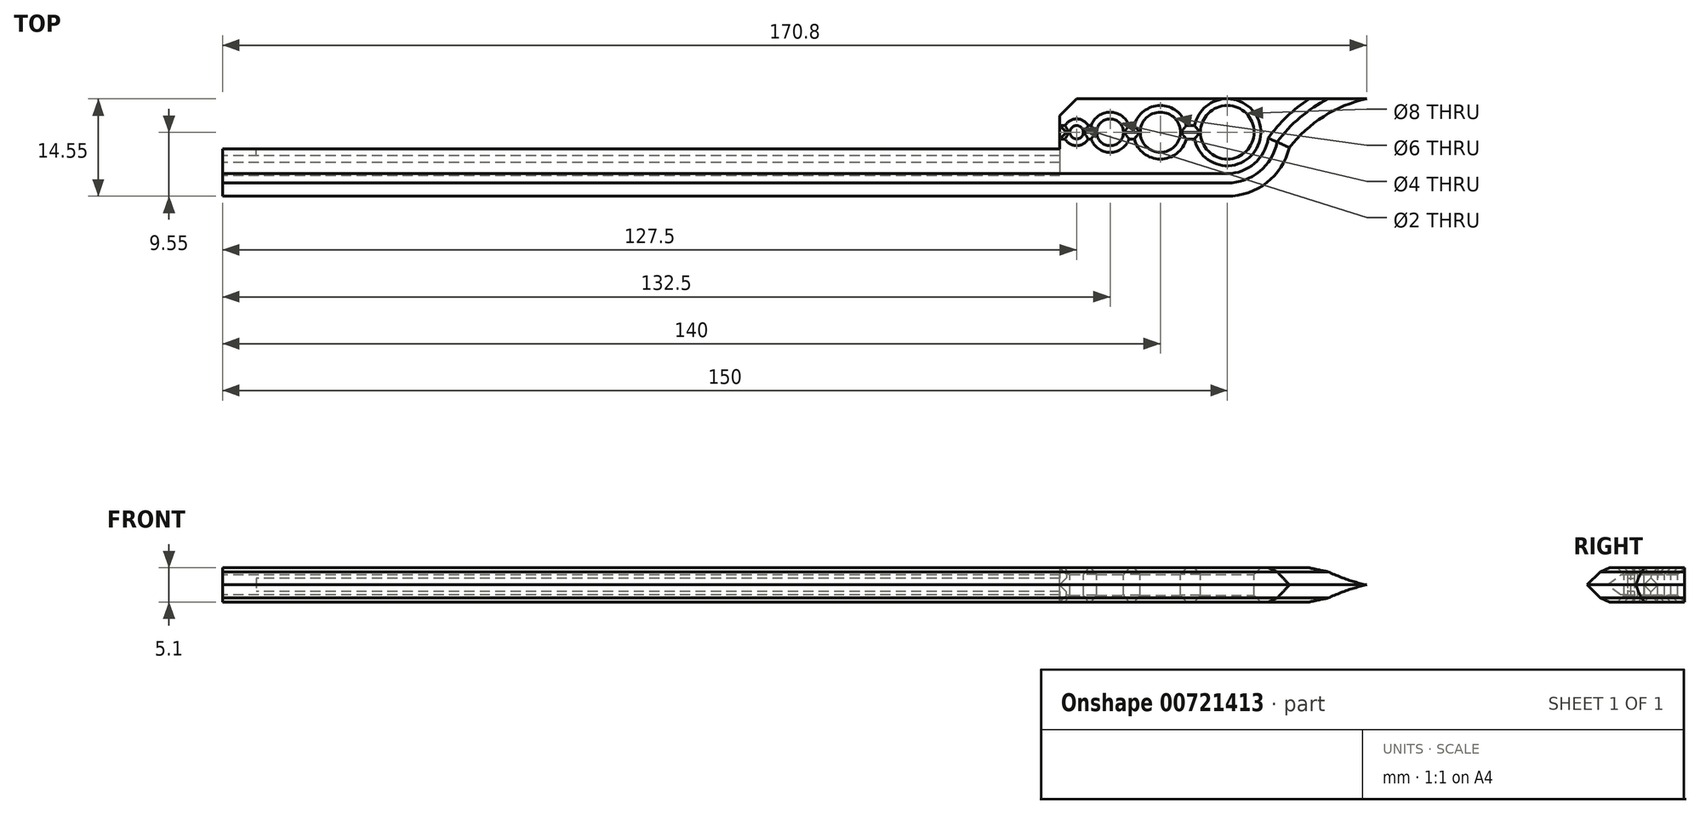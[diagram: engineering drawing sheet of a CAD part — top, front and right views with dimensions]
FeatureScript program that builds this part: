
annotation { "Feature Type Name" : "Feature", "Feature Type Description" : "" }
export const myFeature = defineFeature(function(context is Context, id is Id, definition is map)
    precondition{}
    {
        {
            var Q0;
            Q0=qCreatedBy(makeId("Top.planeOp"),FACE);
            var sketch = newSketch(context, id + "F0", { "sketchPlane" : qUnion([Q0])});
            skLineSegment(sketch, "E0.bottom", {"start": v(125, 0) * mm, "end": v(175, 0) * mm});
            skLineSegment(sketch, "E0.top", {"start": v(0, -15) * mm, "end": v(150, -15) * mm});
            skLineSegment(sketch, "E0.left", {"start": v(0, -7.5) * mm, "end": v(0, -15) * mm});
            skArc(sketch, "E1", {"start": v(150, -15) * mm, "mid": v(156.12, -12.9) * mm, "end": v(159.68, -7.5) * mm});
            skArc(sketch, "E2", {"start": v(175, 0) * mm, "mid": v(166.47, -1.98) * mm, "end": v(159.68, -7.5) * mm});
            skLineSegment(sketch, "E3.top", {"start": v(0, -7.5) * mm, "end": v(125, -7.5) * mm});
            skLineSegment(sketch, "E3.right", {"start": v(125, 0) * mm, "end": v(125, -7.5) * mm});
            skPoint(sketch, "E4.orphan", {"position": v(0, 0) * mm});
            skSolve(sketch);
        }
        {
            var Q0;
            Q0 = qSketchRegion(id + "F0", true);
            extrude(context, id + "F1", {"entities" : qUnion([Q0]), "depth" : 2.55 * mm, "offsetDistance" : 25 * mm});
        }
        {
            var Q0;
            Q0=makeQuery(id+"F1.opExtrude","CAP_EDGE",EDGE,{"disambiguationData":[OSD([sQuery(id+"F0.wireOp",EDGE,"E0.top")])],"isStart":false});
            var Q1;
            Q1=makeQuery(id+"F1.opExtrude","CAP_EDGE",EDGE,{"disambiguationData":[OSD([sQuery(id+"F0.wireOp",EDGE,"E1")])],"isStart":false});
            var Q2;
            Q2=makeQuery(id+"F1.opExtrude","CAP_EDGE",EDGE,{"disambiguationData":[OSD([sQuery(id+"F0.wireOp",EDGE,"E2")])],"isStart":false});
            chamfer(context, id + "F2", {"entities" : qUnion([Q0, Q1, Q2]), "width" : 3 * mm, "tangentPropagation" : true});
        }
        {
            var Q0;
            {var subQ0=sQuery(id+"F0.wireOp",EDGE,"E0.top");Q0=makeQuery(id+"F2.opChamfer","BLEND_EDGE",EDGE,{"blendedFrom":[makeQuery(id+"F1.opExtrude","CAP_EDGE",EDGE,{"disambiguationData":[OSD([subQ0])],"isStart":false}),makeQuery(id+"F1.opExtrude","CAP_FACE",FACE,{"disambiguationData":[OSD([sQuery(id+"F0.wireOp",EDGE,"E0.bottom"),subQ0,sQuery(id+"F0.wireOp",EDGE,"E0.left"),sQuery(id+"F0.wireOp",EDGE,"E1"),sQuery(id+"F0.wireOp",EDGE,"E2"),sQuery(id+"F0.wireOp",EDGE,"E3.top"),sQuery(id+"F0.wireOp",EDGE,"E3.right")])],"isStart":false})],"blendedInto":[makeQuery(id+"F1.opExtrude","CAP_FACE",FACE,{"disambiguationData":[OSD([sQuery(id+"F0.wireOp",EDGE,"E0.bottom"),subQ0,sQuery(id+"F0.wireOp",EDGE,"E0.left"),sQuery(id+"F0.wireOp",EDGE,"E1"),sQuery(id+"F0.wireOp",EDGE,"E2"),sQuery(id+"F0.wireOp",EDGE,"E3.top"),sQuery(id+"F0.wireOp",EDGE,"E3.right")])],"isStart":false})]});}
            var Q1;
            {var subQ0=sQuery(id+"F0.wireOp",EDGE,"E1");Q1=makeQuery(id+"F2.opChamfer","BLEND_EDGE",EDGE,{"blendedFrom":[makeQuery(id+"F1.opExtrude","CAP_EDGE",EDGE,{"disambiguationData":[OSD([subQ0])],"isStart":false}),makeQuery(id+"F1.opExtrude","CAP_FACE",FACE,{"disambiguationData":[OSD([sQuery(id+"F0.wireOp",EDGE,"E0.bottom"),sQuery(id+"F0.wireOp",EDGE,"E0.top"),sQuery(id+"F0.wireOp",EDGE,"E0.left"),subQ0,sQuery(id+"F0.wireOp",EDGE,"E2"),sQuery(id+"F0.wireOp",EDGE,"E3.top"),sQuery(id+"F0.wireOp",EDGE,"E3.right")])],"isStart":false})],"blendedInto":[makeQuery(id+"F1.opExtrude","CAP_FACE",FACE,{"disambiguationData":[OSD([sQuery(id+"F0.wireOp",EDGE,"E0.bottom"),sQuery(id+"F0.wireOp",EDGE,"E0.top"),sQuery(id+"F0.wireOp",EDGE,"E0.left"),subQ0,sQuery(id+"F0.wireOp",EDGE,"E2"),sQuery(id+"F0.wireOp",EDGE,"E3.top"),sQuery(id+"F0.wireOp",EDGE,"E3.right")])],"isStart":false})]});}
            var Q2;
            {var subQ0=sQuery(id+"F0.wireOp",EDGE,"E2");Q2=makeQuery(id+"F2.opChamfer","BLEND_EDGE",EDGE,{"blendedFrom":[makeQuery(id+"F1.opExtrude","CAP_EDGE",EDGE,{"disambiguationData":[OSD([subQ0])],"isStart":false}),makeQuery(id+"F1.opExtrude","CAP_FACE",FACE,{"disambiguationData":[OSD([sQuery(id+"F0.wireOp",EDGE,"E0.bottom"),sQuery(id+"F0.wireOp",EDGE,"E0.top"),sQuery(id+"F0.wireOp",EDGE,"E0.left"),sQuery(id+"F0.wireOp",EDGE,"E1"),subQ0,sQuery(id+"F0.wireOp",EDGE,"E3.top"),sQuery(id+"F0.wireOp",EDGE,"E3.right")])],"isStart":false})],"blendedInto":[makeQuery(id+"F1.opExtrude","CAP_FACE",FACE,{"disambiguationData":[OSD([sQuery(id+"F0.wireOp",EDGE,"E0.bottom"),sQuery(id+"F0.wireOp",EDGE,"E0.top"),sQuery(id+"F0.wireOp",EDGE,"E0.left"),sQuery(id+"F0.wireOp",EDGE,"E1"),subQ0,sQuery(id+"F0.wireOp",EDGE,"E3.top"),sQuery(id+"F0.wireOp",EDGE,"E3.right")])],"isStart":false})]});}
            chamfer(context, id + "F3", {"entities" : qUnion([Q0, Q1, Q2]), "width" : 2 * mm, "tangentPropagation" : true});
        }
        {
            var Q0;
            Q0=makeQuery(id+"F1.opExtrude","SWEPT_BODY",BODY,{"disambiguationData":[OSD([sQuery(id+"F0.wireOp",EDGE,"E0.bottom"),sQuery(id+"F0.wireOp",EDGE,"E0.top"),sQuery(id+"F0.wireOp",EDGE,"E0.left"),sQuery(id+"F0.wireOp",EDGE,"E1"),sQuery(id+"F0.wireOp",EDGE,"E2"),sQuery(id+"F0.wireOp",EDGE,"E3.top"),sQuery(id+"F0.wireOp",EDGE,"E3.right")])]});
            var Q1;
            Q1=makeQuery(id+"F1.opExtrude","CAP_FACE",FACE,{"disambiguationData":[OSD([sQuery(id+"F0.wireOp",EDGE,"E0.bottom"),sQuery(id+"F0.wireOp",EDGE,"E0.top"),sQuery(id+"F0.wireOp",EDGE,"E0.left"),sQuery(id+"F0.wireOp",EDGE,"E1"),sQuery(id+"F0.wireOp",EDGE,"E2"),sQuery(id+"F0.wireOp",EDGE,"E3.top"),sQuery(id+"F0.wireOp",EDGE,"E3.right")])],"isStart":true});
            mirror(context, id + "F4", {"operationType" : NewBodyOperationType.ADD, "entities" : qUnion([Q0]), "mirrorPlane" : qUnion([Q1])});
        }
        {
            var Q0;
            {var subQ0=makeQuery(id+"F1.opExtrude","SWEPT_FACE",FACE,{"disambiguationData":[OSD([sQuery(id+"F0.wireOp",EDGE,"E0.left")])]});Q0=makeQuery(id+"F4.boolean.opBoolean","MERGE",FACE,{"derivedFrom":[subQ0,makeQuery(id+"F4.opPattern","COPY",FACE,{"derivedFrom":subQ0,"instanceName":"1"})]});}
            var sketch = newSketch(context, id + "F5", { "sketchPlane" : qUnion([Q0])});
            skLineSegment(sketch, "E5.bottom", {"start": v(7.5, 1) * mm, "end": v(8.5, 1) * mm});
            skLineSegment(sketch, "E5.top", {"start": v(7.5, -1) * mm, "end": v(8.5, -1) * mm});
            skLineSegment(sketch, "E5.left", {"start": v(7.5, 1) * mm, "end": v(7.5, -1) * mm});
            skLineSegment(sketch, "E6.bottom", {"start": v(8.5, 1.5) * mm, "end": v(9.5, 1.5) * mm});
            skLineSegment(sketch, "E6.top", {"start": v(8.5, -1.5) * mm, "end": v(9.5, -1.5) * mm});
            skLineSegment(sketch, "E6.left", {"start": v(8.5, 1.5) * mm, "end": v(8.5, 1) * mm});
            skLineSegment(sketch, "E7.trimOffspring", {"start": v(8.5, -1) * mm, "end": v(8.5, -1.5) * mm});
            skLineSegment(sketch, "E8", {"start": v(9.5, -1.5) * mm, "end": v(11.5, 0) * mm});
            skLineSegment(sketch, "E9", {"start": v(11.5, 0) * mm, "end": v(9.5, 1.5) * mm});
            skSolve(sketch);
        }
        {
            var Q0;
            Q0 = qSketchRegion(id + "F5", true);
            extrude(context, id + "F6", {"entities" : qUnion([Q0]), "operationType" : NewBodyOperationType.REMOVE, "oppositeDirection" : true, "depth" : 125 * mm, "offsetDistance" : 25 * mm});
        }
        {
            var Q0;
            Q0=makeQuery(id+"F1.opExtrude","CAP_FACE",FACE,{"disambiguationData":[OSD([sQuery(id+"F0.wireOp",EDGE,"E0.bottom"),sQuery(id+"F0.wireOp",EDGE,"E0.top"),sQuery(id+"F0.wireOp",EDGE,"E0.left"),sQuery(id+"F0.wireOp",EDGE,"E1"),sQuery(id+"F0.wireOp",EDGE,"E2"),sQuery(id+"F0.wireOp",EDGE,"E3.top"),sQuery(id+"F0.wireOp",EDGE,"E3.right")])],"isStart":false});
            var sketch = newSketch(context, id + "F7", { "sketchPlane" : qUnion([Q0])});
            skPoint(sketch, "E10", {"position": v(150, -5) * mm});
            skPoint(sketch, "E11", {"position": v(140, -5) * mm});
            skPoint(sketch, "E12", {"position": v(132.5, -5) * mm});
            skPoint(sketch, "E13", {"position": v(127.5, -5) * mm});
            skLineSegment(sketch, "E14.bottom", {"start": v(150, -4) * mm, "end": v(125, -4) * mm});
            skLineSegment(sketch, "E14.top", {"start": v(150, -6) * mm, "end": v(125, -6) * mm});
            skLineSegment(sketch, "E14.left", {"start": v(150, -4) * mm, "end": v(150, -6) * mm});
            skLineSegment(sketch, "E14.right", {"start": v(125, -4) * mm, "end": v(125, -6) * mm});
            skSolve(sketch);
        }
        {
            var Q0;
            Q0=sQuery(id+"F7.wireOp",VERTEX,"E10");
            var Q1;
            Q1=makeQuery(id+"F1.opExtrude","SWEPT_BODY",BODY,{"disambiguationData":[OSD([sQuery(id+"F0.wireOp",EDGE,"E0.bottom"),sQuery(id+"F0.wireOp",EDGE,"E0.top"),sQuery(id+"F0.wireOp",EDGE,"E0.left"),sQuery(id+"F0.wireOp",EDGE,"E1"),sQuery(id+"F0.wireOp",EDGE,"E2"),sQuery(id+"F0.wireOp",EDGE,"E3.top"),sQuery(id+"F0.wireOp",EDGE,"E3.right")])]});
            hole(context, id + "F8", {"style" : HoleStyle.C_SINK, "endStyle" : HoleEndStyle.BLIND, "holeDiameter" : 8 * mm, "cSinkDiameter" : 10 * mm, "cSinkAngle" : 90 * degree, "majorDiameter" : 5 * mm, "holeDepth" : 20 * mm, "isTappedThrough" : true, "tappedDepth" : 12 * mm, "tapClearance" : 3, "locations" : qUnion([Q0]), "scope" : qUnion([Q1])});
        }
        {
            var Q0;
            Q0=sQuery(id+"F7.wireOp",VERTEX,"E11");
            var Q1;
            Q1=makeQuery(id+"F1.opExtrude","SWEPT_BODY",BODY,{"disambiguationData":[OSD([sQuery(id+"F0.wireOp",EDGE,"E0.bottom"),sQuery(id+"F0.wireOp",EDGE,"E0.top"),sQuery(id+"F0.wireOp",EDGE,"E0.left"),sQuery(id+"F0.wireOp",EDGE,"E1"),sQuery(id+"F0.wireOp",EDGE,"E2"),sQuery(id+"F0.wireOp",EDGE,"E3.top"),sQuery(id+"F0.wireOp",EDGE,"E3.right")])]});
            hole(context, id + "F9", {"style" : HoleStyle.C_SINK, "endStyle" : HoleEndStyle.BLIND, "holeDiameter" : 6 * mm, "cSinkDiameter" : 8 * mm, "cSinkAngle" : 90 * degree, "majorDiameter" : 5 * mm, "holeDepth" : 20 * mm, "isTappedThrough" : true, "tappedDepth" : 12 * mm, "tapClearance" : 3, "locations" : qUnion([Q0]), "scope" : qUnion([Q1])});
        }
        {
            var Q0;
            Q0=sQuery(id+"F7.wireOp",VERTEX,"E12");
            var Q1;
            Q1=makeQuery(id+"F1.opExtrude","SWEPT_BODY",BODY,{"disambiguationData":[OSD([sQuery(id+"F0.wireOp",EDGE,"E0.bottom"),sQuery(id+"F0.wireOp",EDGE,"E0.top"),sQuery(id+"F0.wireOp",EDGE,"E0.left"),sQuery(id+"F0.wireOp",EDGE,"E1"),sQuery(id+"F0.wireOp",EDGE,"E2"),sQuery(id+"F0.wireOp",EDGE,"E3.top"),sQuery(id+"F0.wireOp",EDGE,"E3.right")])]});
            hole(context, id + "F10", {"style" : HoleStyle.C_SINK, "endStyle" : HoleEndStyle.BLIND, "holeDiameter" : 4 * mm, "cSinkDiameter" : 6 * mm, "cSinkAngle" : 90 * degree, "majorDiameter" : 5 * mm, "holeDepth" : 20 * mm, "isTappedThrough" : true, "tappedDepth" : 12 * mm, "tapClearance" : 3, "locations" : qUnion([Q0]), "scope" : qUnion([Q1])});
        }
        {
            var Q0;
            Q0=sQuery(id+"F7.wireOp",VERTEX,"E13");
            var Q1;
            Q1=makeQuery(id+"F1.opExtrude","SWEPT_BODY",BODY,{"disambiguationData":[OSD([sQuery(id+"F0.wireOp",EDGE,"E0.bottom"),sQuery(id+"F0.wireOp",EDGE,"E0.top"),sQuery(id+"F0.wireOp",EDGE,"E0.left"),sQuery(id+"F0.wireOp",EDGE,"E1"),sQuery(id+"F0.wireOp",EDGE,"E2"),sQuery(id+"F0.wireOp",EDGE,"E3.top"),sQuery(id+"F0.wireOp",EDGE,"E3.right")])]});
            hole(context, id + "F11", {"style" : HoleStyle.C_SINK, "endStyle" : HoleEndStyle.BLIND, "holeDiameter" : 2 * mm, "cSinkDiameter" : 4 * mm, "cSinkAngle" : 90 * degree, "majorDiameter" : 5 * mm, "holeDepth" : 20 * mm, "isTappedThrough" : true, "tappedDepth" : 12 * mm, "tapClearance" : 3, "locations" : qUnion([Q0]), "scope" : qUnion([Q1])});
        }
        {
            var Q0;
            {var subQ5=sQuery(id+"F7.wireOp",EDGE,"E14.bottom");Q0=makeQuery(id+"F7.imprint","IMPRINT",FACE,{"disambiguationData":[TD([[makeQuery(id+"F7.imprint","IMPRINT",EDGE,{"derivedFrom":subQ5}),-1.0]])]});}
            var sketch = newSketch(context, id + "F12", { "sketchPlane" : qUnion([Q0])});
            skLineSegment(sketch, "E15.bottom", {"start": v(125, -6) * mm, "end": v(150, -6) * mm});
            skLineSegment(sketch, "E15.top", {"start": v(125, -4) * mm, "end": v(150, -4) * mm});
            skLineSegment(sketch, "E15.left", {"start": v(125, -6) * mm, "end": v(125, -4) * mm});
            skLineSegment(sketch, "E15.right", {"start": v(150, -6) * mm, "end": v(150, -4) * mm});
            skSolve(sketch);
        }
        {
            var Q0;
            Q0 = qSketchRegion(id + "F12", true);
            extrude(context, id + "F13", {"entities" : qUnion([Q0]), "operationType" : NewBodyOperationType.REMOVE, "oppositeDirection" : true, "depth" : 1 * mm, "offsetDistance" : 25 * mm, "hasDraft" : true, "draftAngle" : 45 * degree, "draftPullDirection" : true});
        }
        {
            var Q0;
            {var subQ0=makeQuery(id+"F1.opExtrude","SWEPT_FACE",FACE,{"disambiguationData":[OSD([sQuery(id+"F0.wireOp",EDGE,"E3.right")])]});Q0=makeQuery(id+"F6.boolean.opBoolean","MERGE",FACE,{"derivedFrom":[makeQuery(id+"F4.boolean.opBoolean","MERGE",FACE,{"derivedFrom":[subQ0,makeQuery(id+"F4.opPattern","COPY",FACE,{"derivedFrom":subQ0,"instanceName":"1"})]}),makeQuery(id+"F6.opExtrude","CAP_FACE",FACE,{"disambiguationData":[OSD([sQuery(id+"F5.wireOp",EDGE,"E5.bottom"),sQuery(id+"F5.wireOp",EDGE,"E5.top"),sQuery(id+"F5.wireOp",EDGE,"E5.left"),sQuery(id+"F5.wireOp",EDGE,"E6.bottom"),sQuery(id+"F5.wireOp",EDGE,"E6.top"),sQuery(id+"F5.wireOp",EDGE,"E6.left"),sQuery(id+"F5.wireOp",EDGE,"E7.trimOffspring"),sQuery(id+"F5.wireOp",EDGE,"E8"),sQuery(id+"F5.wireOp",EDGE,"E9")])],"isStart":false})]});}
            var sketch = newSketch(context, id + "F14", { "sketchPlane" : qUnion([Q0])});
            skLineSegment(sketch, "E16.bottom", {"start": v(6, 2.55) * mm, "end": v(4, 2.55) * mm});
            skLineSegment(sketch, "E16.top", {"start": v(6, 0.05) * mm, "end": v(4, 0.05) * mm});
            skLineSegment(sketch, "E16.left", {"start": v(6, 2.55) * mm, "end": v(6, 0.05) * mm});
            skLineSegment(sketch, "E16.right", {"start": v(4, 2.55) * mm, "end": v(4, 0.05) * mm});
            skSolve(sketch);
        }
        {
            var Q0;
            Q0 = qSketchRegion(id + "F14", true);
            extrude(context, id + "F15", {"entities" : qUnion([Q0]), "operationType" : NewBodyOperationType.REMOVE, "oppositeDirection" : true, "depth" : 1 * mm, "offsetDistance" : 25 * mm, "hasDraft" : true, "draftAngle" : 45 * degree, "draftPullDirection" : true});
        }
        {
            var Q0;
            Q0=makeQuery(id+"F1.opExtrude","SWEPT_BODY",BODY,{"disambiguationData":[OSD([sQuery(id+"F0.wireOp",EDGE,"E0.bottom"),sQuery(id+"F0.wireOp",EDGE,"E0.top"),sQuery(id+"F0.wireOp",EDGE,"E0.left"),sQuery(id+"F0.wireOp",EDGE,"E1"),sQuery(id+"F0.wireOp",EDGE,"E2"),sQuery(id+"F0.wireOp",EDGE,"E3.top"),sQuery(id+"F0.wireOp",EDGE,"E3.right")])]});
            var Q1;
            Q1=qCreatedBy(makeId("Top.planeOp"),FACE);
            mirror(context, id + "F16", {"operationType" : NewBodyOperationType.INTERSECT, "entities" : qUnion([Q0]), "mirrorPlane" : qUnion([Q1])});
        }
        {
            var Q0;
            {var subQ0=makeQuery(id+"F1.opExtrude","SWEPT_EDGE",EDGE,{"disambiguationData":[OSD([sQuery(id+"F0.wireOp",EDGE,"E0.bottom"),sQuery(id+"F0.wireOp",EDGE,"E3.right")])]});Q0=makeQuery(id+"F4.boolean.opBoolean","MERGE",EDGE,{"derivedFrom":[subQ0,makeQuery(id+"F4.opPattern","COPY",EDGE,{"derivedFrom":subQ0,"instanceName":"1"})]});}
            chamfer(context, id + "F17", {"entities" : qUnion([Q0]), "width" : 2.5 * mm, "tangentPropagation" : true});
        }
        {
            var Q0;
            Q0=makeQuery(id+"F6.boolean.opBoolean","COPY",FACE,{"derivedFrom":makeQuery(id+"F6.opExtrude","SWEPT_FACE",FACE,{"disambiguationData":[OSD([sQuery(id+"F5.wireOp",EDGE,"E5.top")])]})});
            var sketch = newSketch(context, id + "F18", { "sketchPlane" : qUnion([Q0])});
            skLineSegment(sketch, "E17", {"start": v(0, -7.5) * mm, "end": v(5, -7.5) * mm});
            skLineSegment(sketch, "E18", {"start": v(5, -7.5) * mm, "end": v(5, -8.5) * mm});
            skLineSegment(sketch, "E19", {"start": v(5, -8.5) * mm, "end": v(0, -8.5) * mm});
            skLineSegment(sketch, "E20", {"start": v(0, -8.5) * mm, "end": v(0, -7.5) * mm});
            skSolve(sketch);
        }
        {
            var Q0;
            Q0 = qSketchRegion(id + "F18", true);
            extrude(context, id + "F19", {"entities" : qUnion([Q0]), "operationType" : NewBodyOperationType.ADD, "endBound" : BoundingType.UP_TO_NEXT, "depth" : 10 * mm, "offsetDistance" : 25 * mm});
        }
    });
